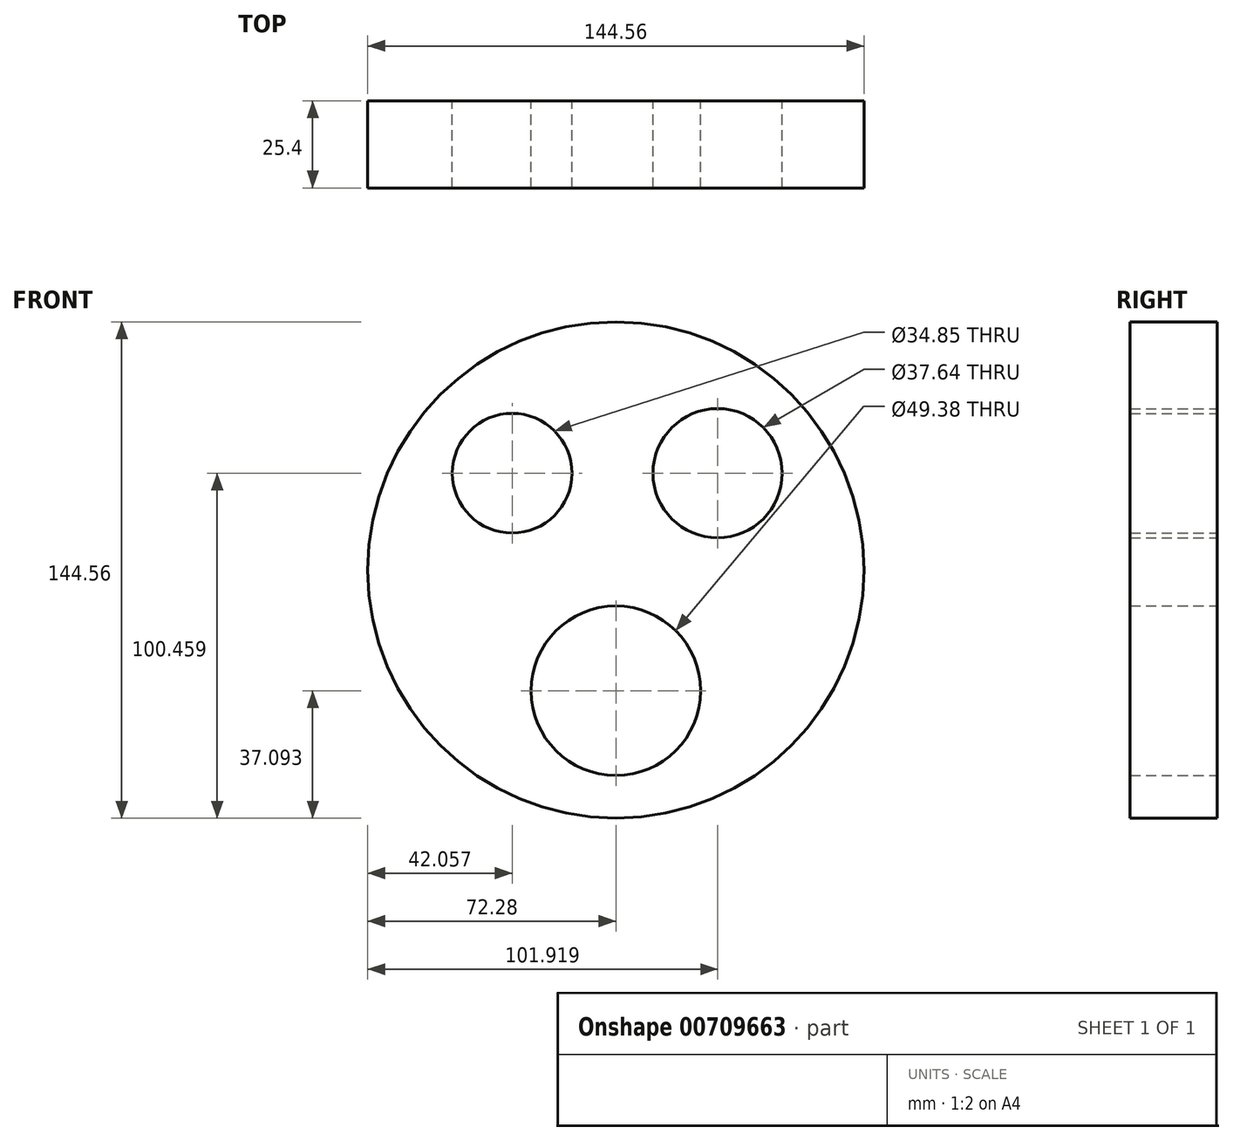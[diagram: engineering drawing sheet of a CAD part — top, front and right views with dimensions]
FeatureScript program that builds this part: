
annotation { "Feature Type Name" : "Feature", "Feature Type Description" : "" }
export const myFeature = defineFeature(function(context is Context, id is Id, definition is map)
    precondition{}
    {
        {
            var Q0;
            Q0=qCreatedBy(makeId("Front.planeOp"),FACE);
            var sketch = newSketch(context, id + "F0", { "sketchPlane" : qUnion([Q0])});
            skCircle(sketch, "E0", {"center": v(0, 0) * mm, "radius": 72.28 * mm});
            skCircle(sketch, "E1", {"center": v(-30.22, 28.18) * mm, "radius": 17.42 * mm});
            skCircle(sketch, "E2", {"center": v(29.64, 28.18) * mm, "radius": 18.82 * mm});
            skCircle(sketch, "E3", {"center": v(0, -35.19) * mm, "radius": 24.69 * mm});
            skSolve(sketch);
        }
        {
            var Q0;
            Q0=makeQuery(id+"F0.imprint","IMPRINT",FACE,{"disambiguationData":[TD([[makeQuery(id+"F0.imprint","IMPRINT",EDGE,{"derivedFrom":sQuery(id+"F0.wireOp",EDGE,"E0")}),1.0]])]});
            extrude(context, id + "F1", {"entities" : qUnion([Q0]), "depth" : 25.4 * mm, "offsetDistance" : 25.4 * mm});
        }
        {
            var Q0;
            Q0=makeQuery(id+"F1.opExtrude","CAP_FACE",FACE,{"disambiguationData":[OSD([sQuery(id+"F0.wireOp",EDGE,"E0"),sQuery(id+"F0.wireOp",EDGE,"E1"),sQuery(id+"F0.wireOp",EDGE,"E2"),sQuery(id+"F0.wireOp",EDGE,"E3")])],"isStart":true});
            extrude(context, id + "F2", {"entities" : qUnion([Q0]), "operationType" : NewBodyOperationType.ADD, "oppositeDirection" : true, "depth" : 11.68 * mm, "offsetDistance" : 25.4 * mm});
        }
    });
